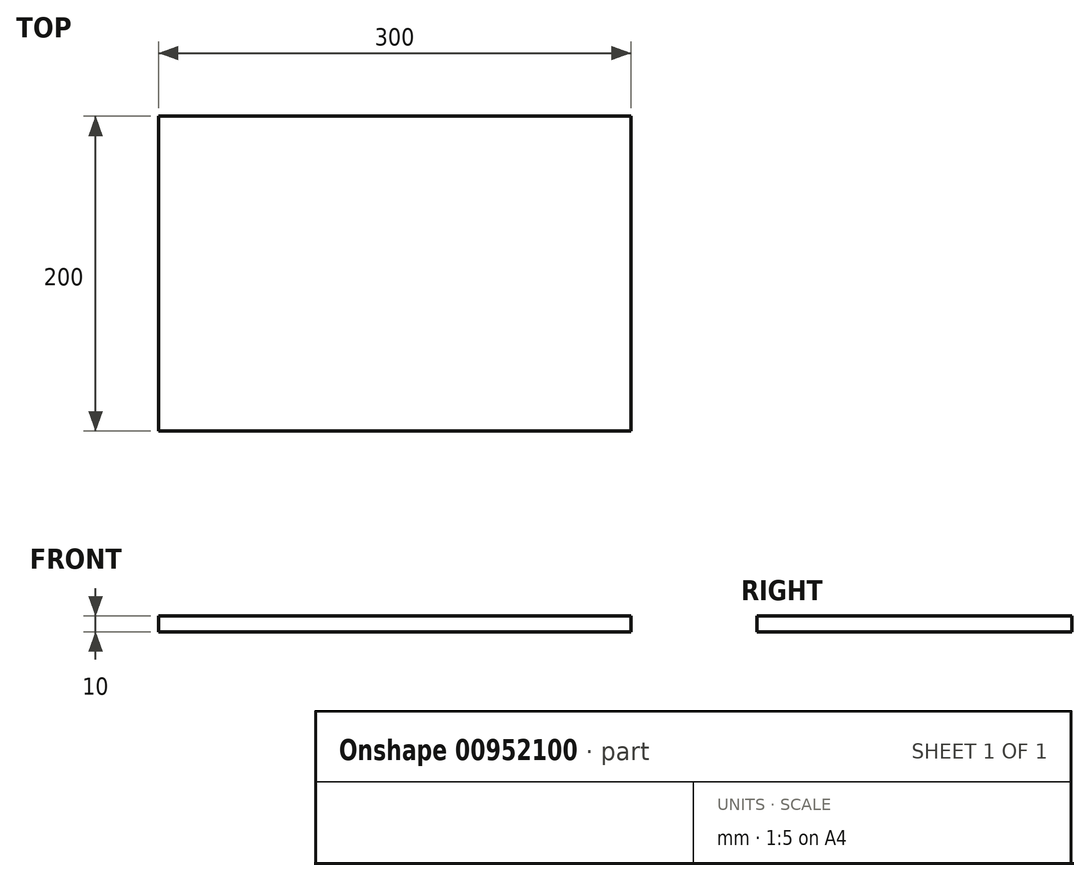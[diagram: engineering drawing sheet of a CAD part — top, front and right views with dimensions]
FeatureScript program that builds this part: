
annotation { "Feature Type Name" : "Feature", "Feature Type Description" : "" }
export const myFeature = defineFeature(function(context is Context, id is Id, definition is map)
    precondition{}
    {
        {
            var Q0;
            Q0=qCreatedBy(makeId("Top.planeOp"),FACE);
            var sketch = newSketch(context, id + "F0", { "sketchPlane" : qUnion([Q0])});
            skLineSegment(sketch, "E0.bottom", {"start": v(-150, 100) * mm, "end": v(150, 100) * mm});
            skLineSegment(sketch, "E0.top", {"start": v(-150, -100) * mm, "end": v(150, -100) * mm});
            skLineSegment(sketch, "E0.left", {"start": v(-150, 100) * mm, "end": v(-150, -100) * mm});
            skLineSegment(sketch, "E0.right", {"start": v(150, 100) * mm, "end": v(150, -100) * mm});
            skPoint(sketch, "E0.middle", {"position": v(0, 0) * mm});
            skSolve(sketch);
        }
        {
            var Q0;
            Q0=makeQuery(id+"F0.imprint","IMPRINT",FACE,{"disambiguationData":[TD([[makeQuery(id+"F0.imprint","IMPRINT",EDGE,{"derivedFrom":sQuery(id+"F0.wireOp",EDGE,"E0.bottom")}),-1.0]])]});
            extrude(context, id + "F1", {"entities" : qUnion([Q0]), "depth" : 10 * mm, "offsetDistance" : 25 * mm});
        }
    });
